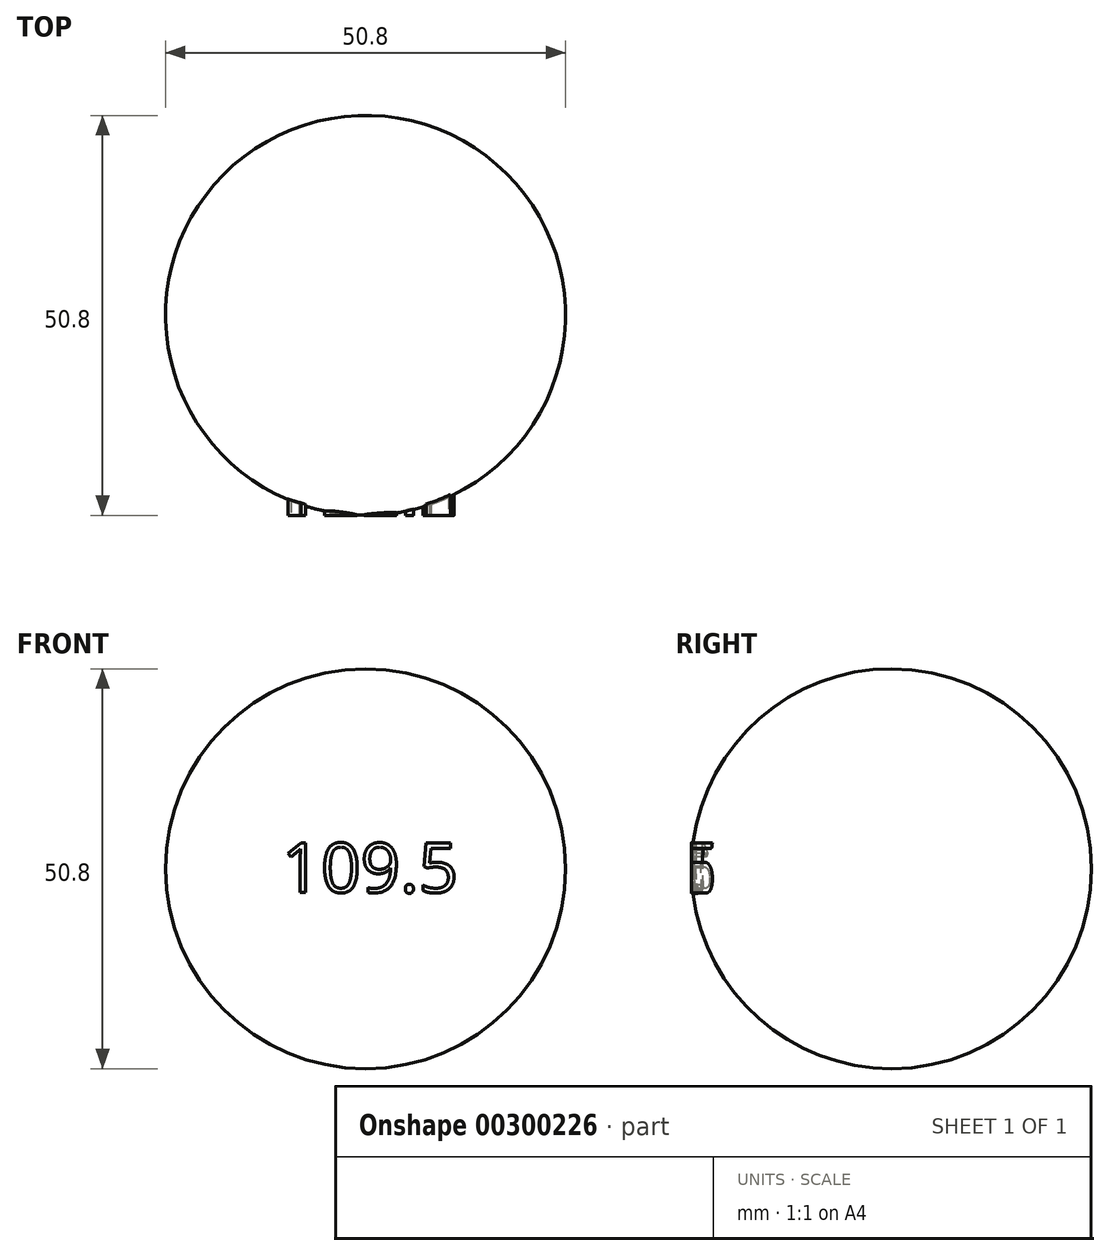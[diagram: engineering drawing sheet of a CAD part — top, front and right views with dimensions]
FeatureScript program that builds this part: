
annotation { "Feature Type Name" : "Feature", "Feature Type Description" : "" }
export const myFeature = defineFeature(function(context is Context, id is Id, definition is map)
    precondition{}
    {
        {
            var Q0;
            Q0=qCreatedBy(makeId("Front.planeOp"),FACE);
            var sketch = newSketch(context, id + "F0", { "sketchPlane" : qUnion([Q0])});
            skArc(sketch, "E0", {"start": v(0, 25.4) * mm, "mid": v(-25.4, 0) * mm, "end": v(0, -25.4) * mm});
            skLineSegment(sketch, "E1", {"start": v(0, 25.4) * mm, "end": v(0, -25.4) * mm});
            skSolve(sketch);
        }
        {
            var Q0;
            Q0=qCreatedBy(makeId("Top.planeOp"),FACE);
            var sketch = newSketch(context, id + "F1", { "sketchPlane" : qUnion([Q0])});
            skCircle(sketch, "E2", {"center": v(0, 0) * mm, "radius": 25.4 * mm});
            skSolve(sketch);
        }
        {
            var Q0;
            Q0=makeQuery(id+"F0.imprint","IMPRINT",FACE,{"disambiguationData":[TD([[makeQuery(id+"F0.imprint","IMPRINT",EDGE,{"derivedFrom":sQuery(id+"F0.wireOp",EDGE,"E0")}),1.0]])]});
            var Q1;
            Q1=sQuery(id+"F1.wireOp",EDGE,"E2");
            revolve(context, id + "F2", {"entities" : qUnion([Q0]), "axis" : qUnion([Q1]), "revolveType" : RevolveType.FULL});
        }
        {
            var Q0;
            Q0=qCreatedBy(makeId("Front.planeOp"),FACE);
            cPlane(context, id + "F3", {"entities" : qUnion([Q0]), "cplaneType" : CPlaneType.OFFSET, "offset" : 25.4 * mm, "width" : 152.4 * mm, "height" : 152.4 * mm});
        }
        {
            var Q0;
            Q0=qCreatedBy(id+"F3.planeOp",FACE);
            var sketch = newSketch(context, id + "F4", { "sketchPlane" : qUnion([Q0])});
            skText(sketch, "E3", { "text": "109.5\n", "fontName": "OpenSans-Regular.ttf"});
            const initialGuessF4  = {"E3": [-0.01066, -0.00301, 1, 0, 0.00632]};
            skSetInitialGuess(sketch, initialGuessF4);
            skSolve(sketch);
        }
        {
            var Q0;
            Q0 = qSketchRegion(id + "F4", true);
            extrude(context, id + "F5", {"entities" : qUnion([Q0]), "operationType" : NewBodyOperationType.ADD, "oppositeDirection" : true, "depth" : 12.7 * mm});
        }
        {
            var Q0;
            Q0=qCreatedBy(makeId("Top.planeOp"),FACE);
            cPlane(context, id + "F6", {"entities" : qUnion([Q0]), "cplaneType" : CPlaneType.OFFSET, "offset" : 25.4 * mm, "width" : 152.4 * mm, "height" : 152.4 * mm});
        }
    });
